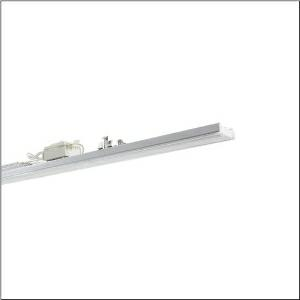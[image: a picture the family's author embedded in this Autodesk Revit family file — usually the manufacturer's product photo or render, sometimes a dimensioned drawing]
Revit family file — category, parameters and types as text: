
# Revit family: licross_21_recessed_ho_52te12dv4l2m
name_source: partatom
category: Lighting Fixtures
units: mm (PartAtom-declared; Revit-internal decimal feet)

## family parameters
Cut with Voids When Loaded = No
Host = Face
Light Source = No
Part Type = Normal
Room Calculation Point = No
Round Connector Dimension = Use Diameter
Shared = No

## types (1)
- --- (1 x LED, 22710 lm, 125.6 W, 4000K)
    Apparent Load = 126 VA
    CIE Flux Codes = 69 91 98 100 100
    Color Rendering = 80
    Color Temperature = 4000K
    Default Elevation = 1800 mm
    Description = Licross 21 Recessed HO, luminaire insert, of sheet steel, galvanised, coil coated, white, length: 2.250mm, width: 66mm, height: 67mm, LED rated luminous flux: 22.710lm, light colour: 840, SDCM (Standard Deviation of Colour Matching)MacAdam ≤ 3 SDCM (initial), control gear: DALI 2, with plug, 5-pole, with phase selection, mains connection: 220..240V, AC, 50/60Hz, rated input power: 126W, internal wiring halogen-free, primary optical cover: cover, of PMMA, light emission: direct distribution, primary light characteristic: symmetric, protection rating (complete): IP54, insulation class (complete): insulation class I (protective earthing), certification: CE, ENEC, VDE, UKCA, protection symbol: D if used in an environment with non-conductive dust loads with corresponding accessories, impact resistance: IK06, permissible ambient temperature for indoor applications: -40..+30°C, corresponds to IFS (International Featured Standards) requirements for safety and quality in the food industry, reducing of maximum allowable ambient temperature of 5°C with ceiling mounting, LABS conformity tested according to VDMA 24364:2018-05, The light source and the operating device comply with the requirements of the Ecodesign Regulation (EU) 2019/2020 and are replaceable in accordance with this regulation, packaging unit: 1 piece
    Height = 58 mm
    Lamp = 1 x LED
    Lamp Light Flux = 22710 lm
    Lamp Power = 125.6 W
    Lamp count = 1
    Length = 2250 mm
    Luminous efficacy = 181 lm/W
    Manufacturer = Siteco
    ModVariant = No
    Model = 52TE12DV4L2M
    Mounting Place = Ceiling
    Mounting Type = Pendant
    Number of Poles = 1
    OnlyDefault = Yes
    Power Factor = 1
    Product Name = Licross 21 Recessed HO
    Product group = luminaire insert | ceiling pendant
    ProductGroupID = 901
    Protection Class = Protection class I
    Protection Degree = IP 54
    RLX_Detail_Level = 1
    RLX_Emergency_Light_Flux = 0 lm
    RLX_Emergency_Type = 0
    RLX_Emergency_Type_DB = No
    RlxData = <blob elided: 29913 chars, md5=b2e13b99>
    Socket = socket
    Standby Power = 0 W
    System Light Flux = 22710 lm
    System Power = 126 W
    Type Comments = factory setting: luminous flux: 100 % | dim-lin: 254 | 489 mA
    Type Image = l_1296930.jpg
    URL = http://relux.com
    VarID = @adj_116809
    Voltage = 0 V
    Weight = 0.00 kg
    Width = 66 mm

## geometry (parser evidence)
native form markers: Blend x4, Sweep x10
no freeform markers — native parametric forms only
